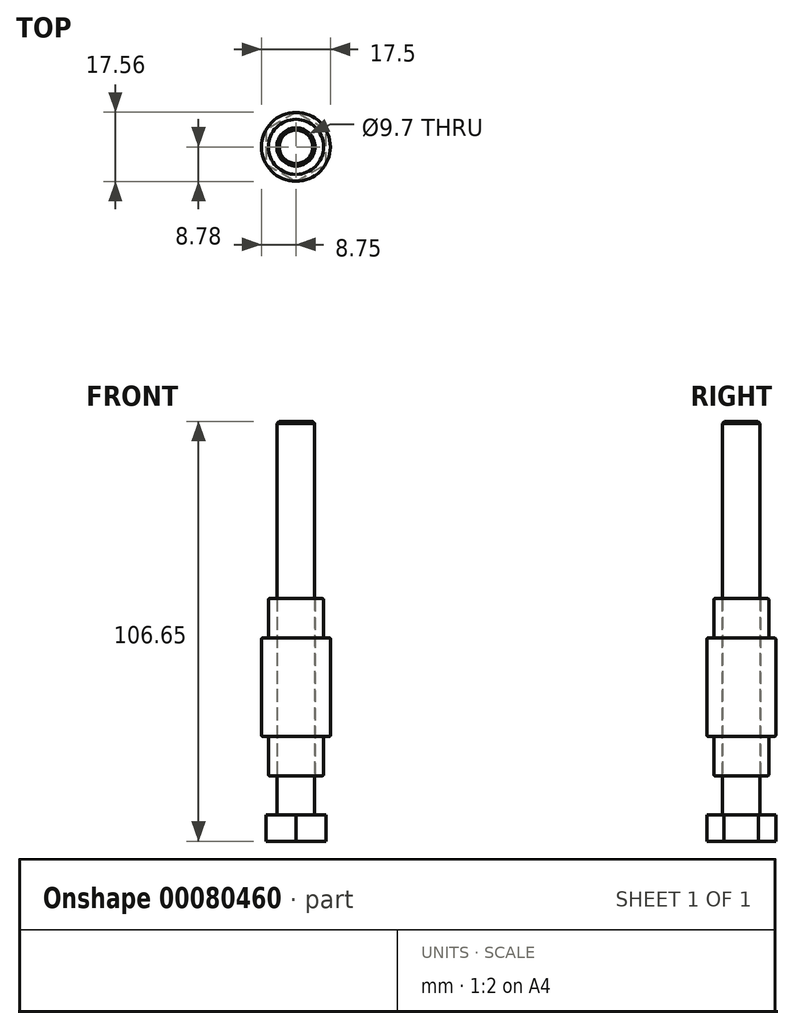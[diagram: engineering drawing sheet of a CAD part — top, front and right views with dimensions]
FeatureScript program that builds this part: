
annotation { "Feature Type Name" : "Feature", "Feature Type Description" : "" }
export const myFeature = defineFeature(function(context is Context, id is Id, definition is map)
    precondition{}
    {
        {
            var Q0;
            Q0=qCreatedBy(makeId("Top.planeOp"),FACE);
            var sketch = newSketch(context, id + "F0", { "sketchPlane" : qUnion([Q0])});
            skCircle(sketch, "E0", {"center": v(0, 0) * mm, "radius": 4.75 * mm});
            skSolve(sketch);
        }
        {
            var Q0;
            Q0 = qSketchRegion(id + "F0", true);
            extrude(context, id + "F1", {"entities" : qUnion([Q0]), "depth" : 100 * mm});
        }
        {
            var Q0;
            Q0=makeQuery(id+"F1.opExtrude","CAP_FACE",FACE,{"disambiguationData":[OSD([sQuery(id+"F0.wireOp",EDGE,"E0")])],"isStart":true});
            var sketch = newSketch(context, id + "F2", { "sketchPlane" : qUnion([Q0])});
            skCircle(sketch, "E1.cCircle", {"center": v(0, 0) * mm, "radius": 7.6 * mm, "construction": true});
            skLineSegment(sketch, "E1.0", {"start": v(7.6, 4.39) * mm, "end": v(7.6, -4.39) * mm});
            skLineSegment(sketch, "E1.1", {"start": v(7.6, -4.39) * mm, "end": v(0, -8.78) * mm});
            skLineSegment(sketch, "E1.2", {"start": v(0, -8.78) * mm, "end": v(-7.6, -4.39) * mm});
            skLineSegment(sketch, "E1.3", {"start": v(-7.6, -4.39) * mm, "end": v(-7.6, 4.39) * mm});
            skLineSegment(sketch, "E1.4", {"start": v(-7.6, 4.39) * mm, "end": v(0, 8.78) * mm});
            skLineSegment(sketch, "E1.5", {"start": v(0, 8.78) * mm, "end": v(7.6, 4.39) * mm});
            skPoint(sketch, "E1.0.midPoint", {"position": v(7.6, 0) * mm});
            skSolve(sketch);
        }
        {
            var Q0;
            Q0 = qSketchRegion(id + "F2", true);
            extrude(context, id + "F3", {"entities" : qUnion([Q0]), "operationType" : NewBodyOperationType.ADD, "depth" : (9.5 * 0.7) * mm});
        }
        {
            var Q0;
            Q0=makeQuery(id+"F1.opExtrude","CAP_EDGE",EDGE,{"disambiguationData":[OSD([sQuery(id+"F0.wireOp",EDGE,"E0")])],"isStart":false});
            var Q1;
            Q1=makeQuery(id+"F1.opExtrude","CAP_EDGE",EDGE,{"disambiguationData":[OSD([sQuery(id+"F0.wireOp",EDGE,"E0")])],"isStart":true});
            chamfer(context, id + "F4", {"entities" : qUnion([Q0, Q1]), "width" : 0.5 * mm, "tangentPropagation" : true});
        }
        {
            var Q0;
            Q0=qCreatedBy(makeId("Front.planeOp"),FACE);
            var sketch = newSketch(context, id + "F5", { "sketchPlane" : qUnion([Q0])});
            skLineSegment(sketch, "E2", {"start": v(0, 0) * mm, "end": v(0, 41.36) * mm, "construction": true});
            skLineSegment(sketch, "E3", {"start": v(4.85, 55) * mm, "end": v(4.85, 10) * mm});
            skLineSegment(sketch, "E4", {"start": v(4.85, 10) * mm, "end": v(7, 10) * mm});
            skLineSegment(sketch, "E5", {"start": v(7, 10) * mm, "end": v(7, 20) * mm});
            skLineSegment(sketch, "E6", {"start": v(7, 20) * mm, "end": v(8.75, 20) * mm});
            skLineSegment(sketch, "E7", {"start": v(8.75, 20) * mm, "end": v(8.75, 45) * mm});
            skLineSegment(sketch, "E8", {"start": v(8.75, 45) * mm, "end": v(7, 45) * mm});
            skLineSegment(sketch, "E9", {"start": v(7, 45) * mm, "end": v(7, 55) * mm});
            skLineSegment(sketch, "E10", {"start": v(7, 55) * mm, "end": v(4.85, 55) * mm});
            skSolve(sketch);
        }
        {
            var Q0;
            Q0 = qSketchRegion(id + "F5", true);
            var Q1;
            Q1=sQuery(id+"F5.wireOp",EDGE,"E2");
            revolve(context, id + "F6", {"entities" : qUnion([Q0]), "axis" : qUnion([Q1]), "revolveType" : RevolveType.FULL});
        }
        {
            var Q0;
            Q0=makeQuery(id+"F6.opRevolve","SWEPT_EDGE",EDGE,{"disambiguationData":[OSD([sQuery(id+"F5.wireOp",EDGE,"E4"),sQuery(id+"F5.wireOp",EDGE,"E5")])]});
            var Q1;
            Q1=makeQuery(id+"F6.opRevolve","SWEPT_EDGE",EDGE,{"disambiguationData":[OSD([sQuery(id+"F5.wireOp",EDGE,"E5"),sQuery(id+"F5.wireOp",EDGE,"E6")])]});
            var Q2;
            Q2=makeQuery(id+"F6.opRevolve","SWEPT_EDGE",EDGE,{"disambiguationData":[OSD([sQuery(id+"F5.wireOp",EDGE,"E6"),sQuery(id+"F5.wireOp",EDGE,"E7")])]});
            var Q3;
            Q3=makeQuery(id+"F6.opRevolve","SWEPT_EDGE",EDGE,{"disambiguationData":[OSD([sQuery(id+"F5.wireOp",EDGE,"E7"),sQuery(id+"F5.wireOp",EDGE,"E8")])]});
            var Q4;
            Q4=makeQuery(id+"F6.opRevolve","SWEPT_EDGE",EDGE,{"disambiguationData":[OSD([sQuery(id+"F5.wireOp",EDGE,"E8"),sQuery(id+"F5.wireOp",EDGE,"E9")])]});
            var Q5;
            Q5=makeQuery(id+"F6.opRevolve","SWEPT_EDGE",EDGE,{"disambiguationData":[OSD([sQuery(id+"F5.wireOp",EDGE,"E9"),sQuery(id+"F5.wireOp",EDGE,"E10")])]});
            var Q6;
            Q6=makeQuery(id+"F6.opRevolve","SWEPT_EDGE",EDGE,{"disambiguationData":[OSD([sQuery(id+"F5.wireOp",EDGE,"E3"),sQuery(id+"F5.wireOp",EDGE,"E10")])]});
            var Q7;
            Q7=makeQuery(id+"F6.opRevolve","SWEPT_EDGE",EDGE,{"disambiguationData":[OSD([sQuery(id+"F5.wireOp",EDGE,"E3"),sQuery(id+"F5.wireOp",EDGE,"E4")])]});
            fillet(context, id + "F7", {"entities" : qUnion([Q0, Q1, Q2, Q3, Q4, Q5, Q6, Q7]), "radius" : 0.3 * mm, "tangentPropagation" : true, "allowEdgeOverflow" : false});
        }
    });
